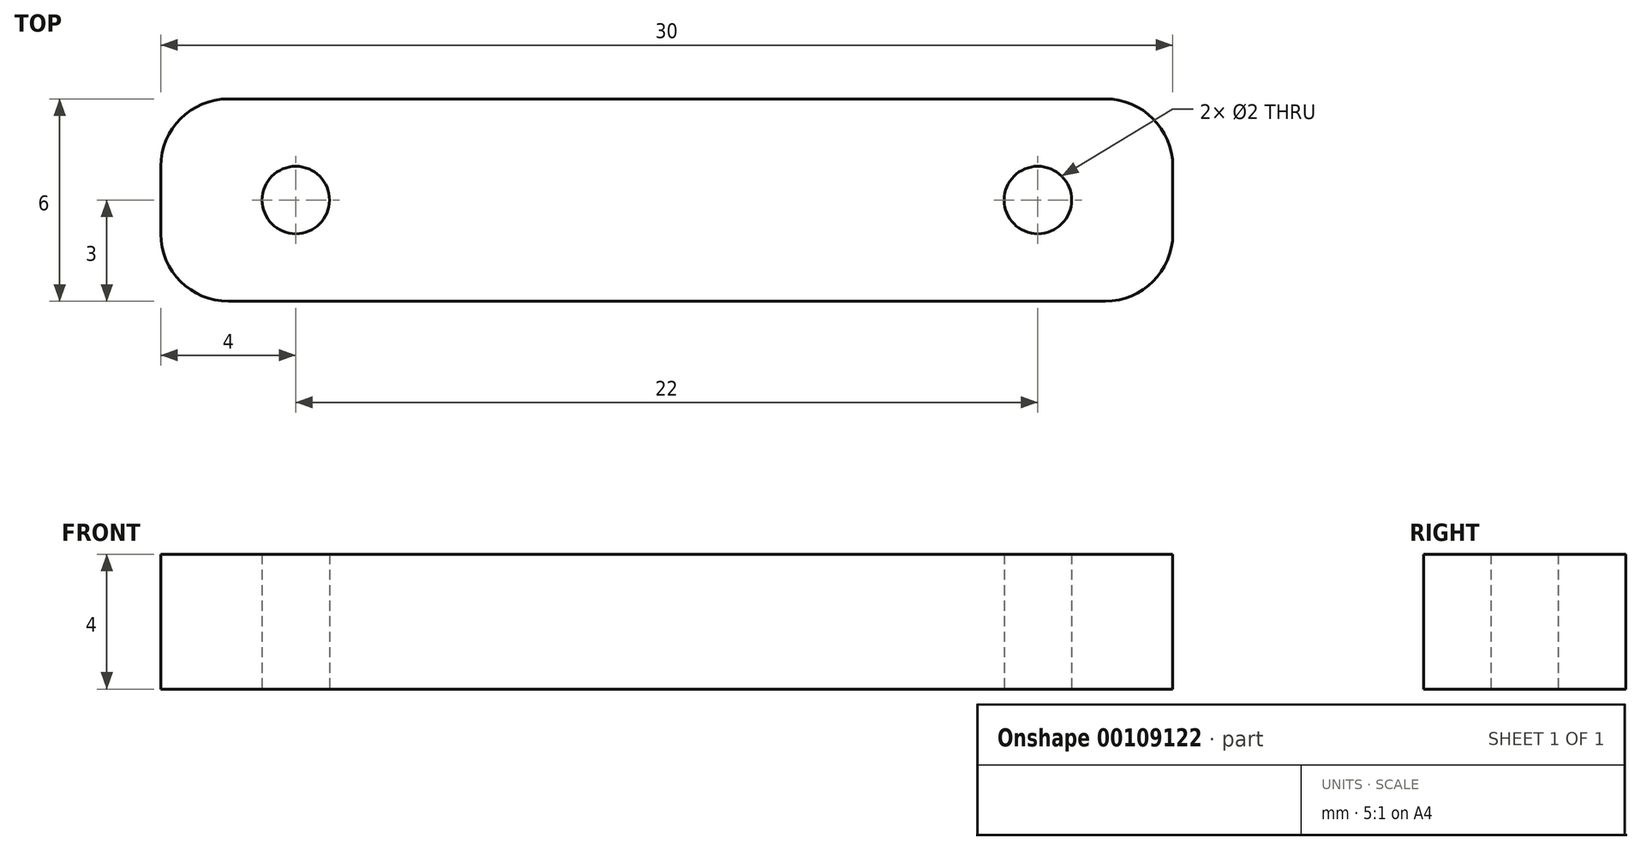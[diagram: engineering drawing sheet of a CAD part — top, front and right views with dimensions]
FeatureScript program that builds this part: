
annotation { "Feature Type Name" : "Feature", "Feature Type Description" : "" }
export const myFeature = defineFeature(function(context is Context, id is Id, definition is map)
    precondition{}
    {
        {
            var Q0;
            Q0=qCreatedBy(makeId("Top.planeOp"),FACE);
            var sketch = newSketch(context, id + "F0", { "sketchPlane" : qUnion([Q0])});
            skLineSegment(sketch, "E0.bottom", {"start": v(15, 3) * mm, "end": v(-15, 3) * mm});
            skLineSegment(sketch, "E0.top", {"start": v(15, -3) * mm, "end": v(-15, -3) * mm});
            skLineSegment(sketch, "E0.left", {"start": v(15, 3) * mm, "end": v(15, -3) * mm});
            skLineSegment(sketch, "E0.right", {"start": v(-15, 3) * mm, "end": v(-15, -3) * mm});
            skPoint(sketch, "E0.middle", {"position": v(0, 0) * mm});
            skCircle(sketch, "E1", {"center": v(-11, 0) * mm, "radius": 1 * mm});
            skCircle(sketch, "E2", {"center": v(11, 0) * mm, "radius": 1 * mm});
            skSolve(sketch);
        }
        {
            var Q0;
            Q0=makeQuery(id+"F0.imprint","IMPRINT",FACE,{"disambiguationData":[TD([[makeQuery(id+"F0.imprint","IMPRINT",EDGE,{"derivedFrom":sQuery(id+"F0.wireOp",EDGE,"E0.bottom")}),1.0]])]});
            extrude(context, id + "F1", {"entities" : qUnion([Q0]), "depth" : 4 * mm});
        }
        {
            var Q0;
            Q0=makeQuery(id+"F1.opExtrude","SWEPT_EDGE",EDGE,{"disambiguationData":[OSD([sQuery(id+"F0.wireOp",EDGE,"E0.bottom"),sQuery(id+"F0.wireOp",EDGE,"E0.right")])]});
            var Q1;
            Q1=makeQuery(id+"F1.opExtrude","SWEPT_EDGE",EDGE,{"disambiguationData":[OSD([sQuery(id+"F0.wireOp",EDGE,"E0.top"),sQuery(id+"F0.wireOp",EDGE,"E0.right")])]});
            var Q2;
            Q2=makeQuery(id+"F1.opExtrude","SWEPT_EDGE",EDGE,{"disambiguationData":[OSD([sQuery(id+"F0.wireOp",EDGE,"E0.top"),sQuery(id+"F0.wireOp",EDGE,"E0.left")])]});
            var Q3;
            Q3=makeQuery(id+"F1.opExtrude","SWEPT_EDGE",EDGE,{"disambiguationData":[OSD([sQuery(id+"F0.wireOp",EDGE,"E0.bottom"),sQuery(id+"F0.wireOp",EDGE,"E0.left")])]});
            fillet(context, id + "F2", {"entities" : qUnion([Q0, Q1, Q2, Q3]), "radius" : 2 * mm, "tangentPropagation" : true, "allowEdgeOverflow" : false});
        }
    });
